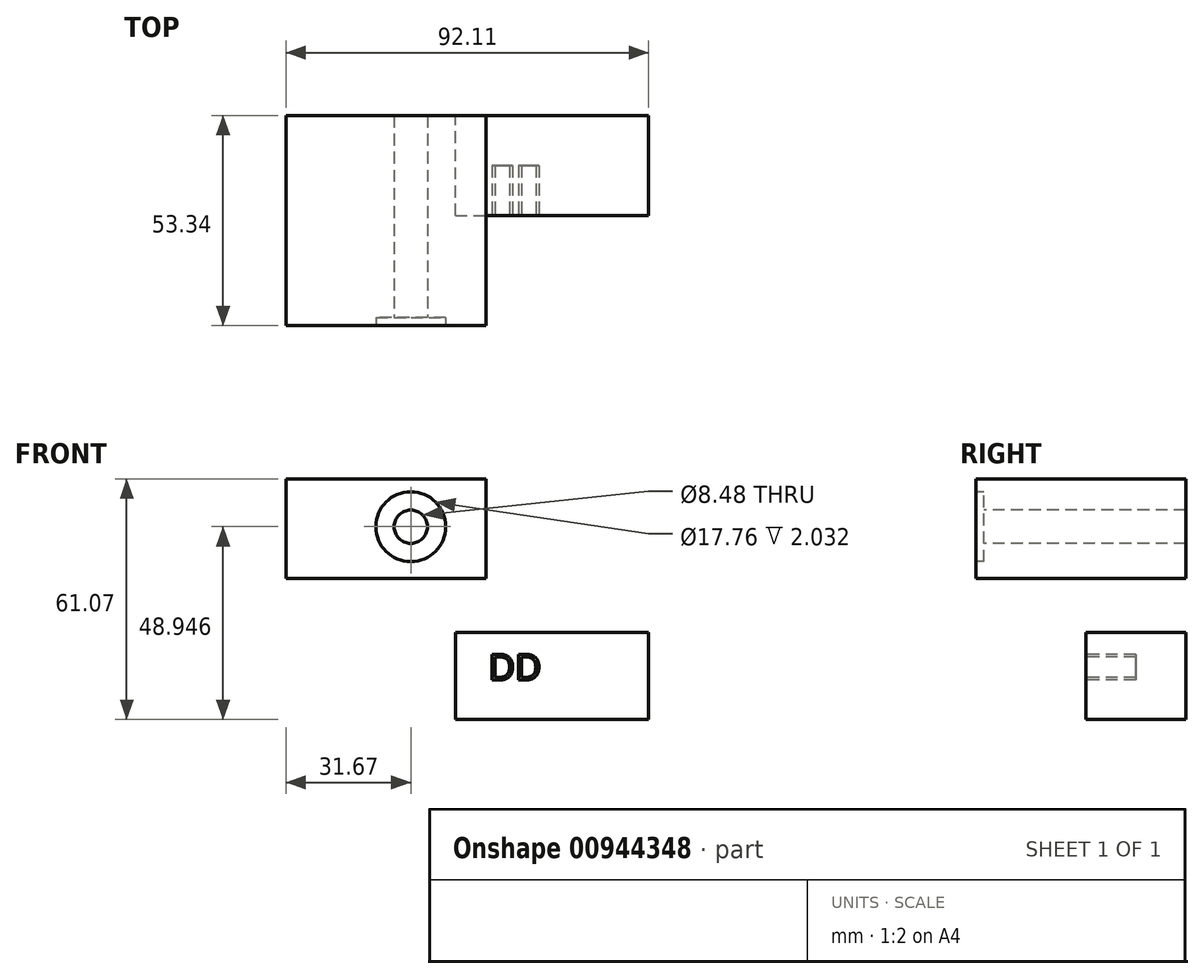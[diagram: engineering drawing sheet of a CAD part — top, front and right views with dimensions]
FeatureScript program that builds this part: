
annotation { "Feature Type Name" : "Feature", "Feature Type Description" : "" }
export const myFeature = defineFeature(function(context is Context, id is Id, definition is map)
    precondition{}
    {
        {
            var Q0;
            Q0=qCreatedBy(makeId("Front.planeOp"),FACE);
            var sketch = newSketch(context, id + "F0", { "sketchPlane" : qUnion([Q0])});
            skLineSegment(sketch, "E0.bottom", {"start": v(-26.4, 16.27) * mm, "end": v(22.7, 16.27) * mm});
            skLineSegment(sketch, "E0.top", {"start": v(-26.4, -5.77) * mm, "end": v(22.7, -5.77) * mm});
            skLineSegment(sketch, "E0.left", {"start": v(-26.4, 16.27) * mm, "end": v(-26.4, -5.77) * mm});
            skLineSegment(sketch, "E0.right", {"start": v(22.7, 16.27) * mm, "end": v(22.7, -5.77) * mm});
            skSolve(sketch);
        }
        {
            var Q0;
            Q0 = qSketchRegion(id + "F0", true);
            extrude(context, id + "F1", {"entities" : qUnion([Q0]), "depth" : 25.4 * mm, "offsetDistance" : 25.4 * mm});
        }
        {
            var Q0;
            Q0=makeQuery(id+"F1.opExtrude","CAP_FACE",FACE,{"disambiguationData":[OSD([sQuery(id+"F0.wireOp",EDGE,"E0.bottom"),sQuery(id+"F0.wireOp",EDGE,"E0.top"),sQuery(id+"F0.wireOp",EDGE,"E0.left"),sQuery(id+"F0.wireOp",EDGE,"E0.right")])],"isStart":false});
            var sketch = newSketch(context, id + "F2", { "sketchPlane" : qUnion([Q0])});
            skText(sketch, "E1", { "text": "DD", "fontName": "OpenSans-Regular.ttf"});
            const initialGuessF2  = {"E1": [-0.01797, 0.00422, 1, 0, 0.00659]};
            skSetInitialGuess(sketch, initialGuessF2);
            skSolve(sketch);
        }
        {
            var Q0;
            Q0 = qSketchRegion(id + "F2", true);
            extrude(context, id + "F3", {"entities" : qUnion([Q0]), "operationType" : NewBodyOperationType.REMOVE, "oppositeDirection" : true, "depth" : 12.7 * mm, "offsetDistance" : 25.4 * mm});
        }
        {
            var Q0;
            Q0=qCreatedBy(makeId("Front.planeOp"),FACE);
            var sketch = newSketch(context, id + "F4", { "sketchPlane" : qUnion([Q0])});
            skLineSegment(sketch, "E2.bottom", {"start": v(-69.4, 55.3) * mm, "end": v(-18.67, 55.3) * mm});
            skLineSegment(sketch, "E2.top", {"start": v(-69.4, 30.06) * mm, "end": v(-18.67, 30.06) * mm});
            skLineSegment(sketch, "E2.left", {"start": v(-69.4, 55.3) * mm, "end": v(-69.4, 30.06) * mm});
            skLineSegment(sketch, "E2.right", {"start": v(-18.67, 55.3) * mm, "end": v(-18.67, 30.06) * mm});
            skSolve(sketch);
        }
        {
            var Q0;
            Q0 = qSketchRegion(id + "F4", true);
            extrude(context, id + "F5", {"entities" : qUnion([Q0]), "depth" : 53.34 * mm, "offsetDistance" : 25.4 * mm});
        }
        {
            var Q0;
            Q0=makeQuery(id+"F5.opExtrude","CAP_FACE",FACE,{"disambiguationData":[OSD([sQuery(id+"F4.wireOp",EDGE,"E2.bottom"),sQuery(id+"F4.wireOp",EDGE,"E2.top"),sQuery(id+"F4.wireOp",EDGE,"E2.left"),sQuery(id+"F4.wireOp",EDGE,"E2.right")])],"isStart":false});
            var sketch = newSketch(context, id + "F6", { "sketchPlane" : qUnion([Q0])});
            skCircle(sketch, "E3", {"center": v(-37.74, 43.18) * mm, "radius": 4.24 * mm});
            skCircle(sketch, "E4", {"center": v(-37.74, 43.18) * mm, "radius": 8.88 * mm});
            skSolve(sketch);
        }
        {
            var Q0;
            Q0=makeQuery(id+"F6.imprint","IMPRINT",FACE,{"disambiguationData":[TD([[makeQuery(id+"F6.imprint","IMPRINT",EDGE,{"derivedFrom":sQuery(id+"F6.wireOp",EDGE,"E3")}),1.0]])]});
            extrude(context, id + "F7", {"entities" : qUnion([Q0]), "operationType" : NewBodyOperationType.REMOVE, "endBound" : BoundingType.THROUGH_ALL, "oppositeDirection" : true, "depth" : 25.4 * mm, "offsetDistance" : 25.4 * mm});
        }
        {
            var Q0;
            Q0=makeQuery(id+"F6.imprint","IMPRINT",FACE,{"disambiguationData":[TD([[makeQuery(id+"F6.imprint","IMPRINT",EDGE,{"derivedFrom":sQuery(id+"F6.wireOp",EDGE,"E3")}),-1.0]])]});
            extrude(context, id + "F8", {"entities" : qUnion([Q0]), "operationType" : NewBodyOperationType.REMOVE, "oppositeDirection" : true, "depth" : 2.03 * mm, "offsetDistance" : 25.4 * mm});
        }
    });
